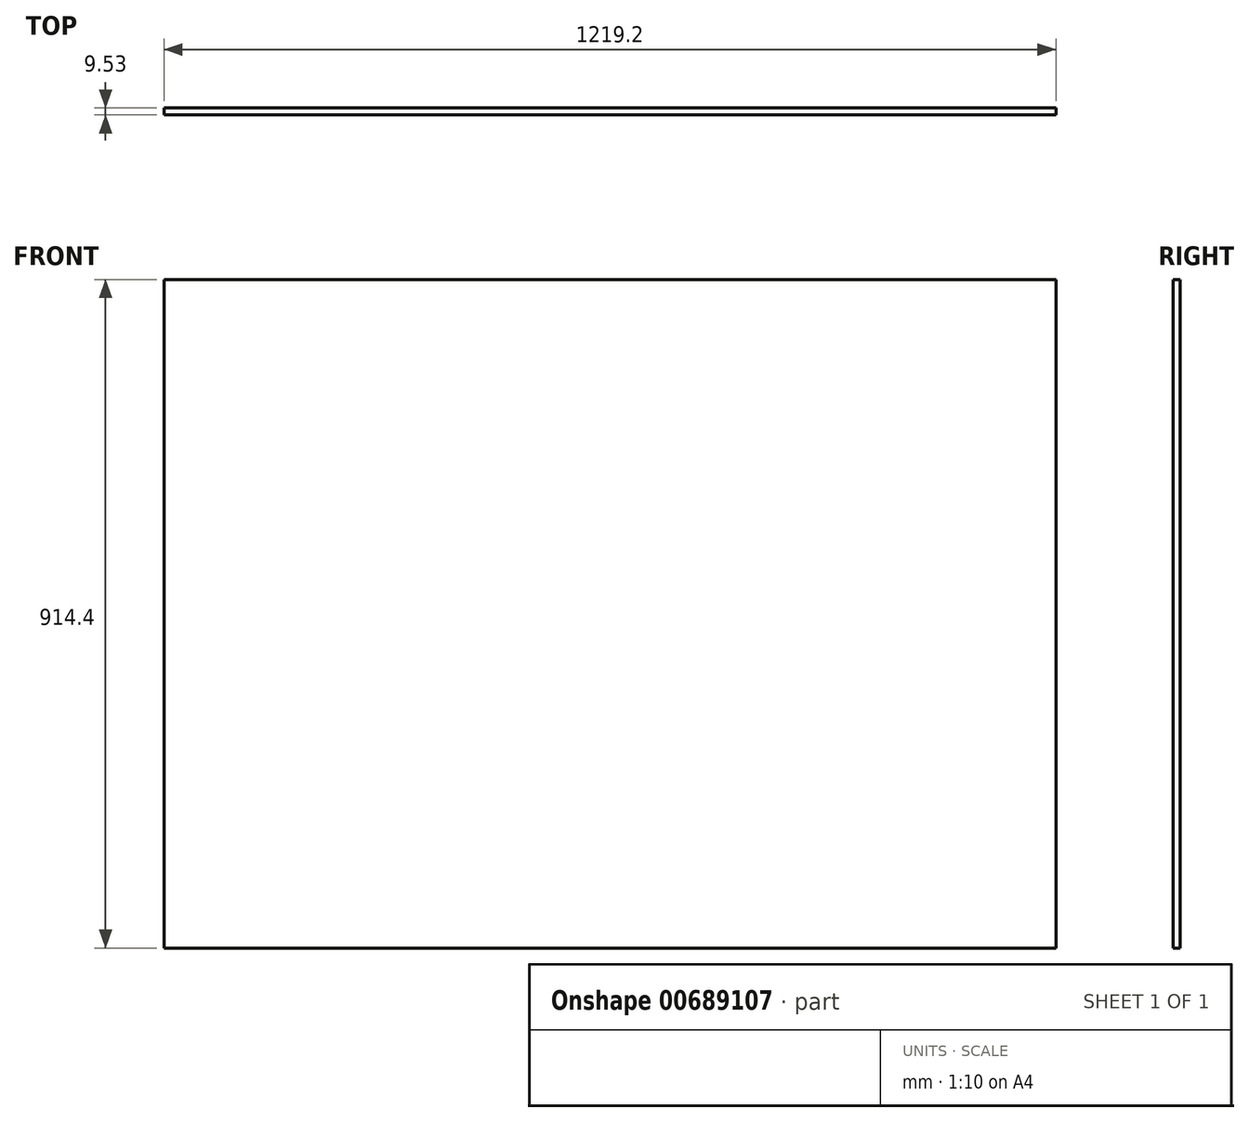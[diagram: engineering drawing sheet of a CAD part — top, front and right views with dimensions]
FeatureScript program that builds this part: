
annotation { "Feature Type Name" : "Feature", "Feature Type Description" : "" }
export const myFeature = defineFeature(function(context is Context, id is Id, definition is map)
    precondition{}
    {
        {
            var Q0;
            Q0=qCreatedBy(makeId("Front.planeOp"),FACE);
            var sketch = newSketch(context, id + "F0", { "sketchPlane" : qUnion([Q0])});
            skLineSegment(sketch, "E0.bottom", {"start": v(-609.6, 457.2) * mm, "end": v(609.6, 457.2) * mm});
            skLineSegment(sketch, "E0.top", {"start": v(-609.6, -457.2) * mm, "end": v(609.6, -457.2) * mm});
            skLineSegment(sketch, "E0.left", {"start": v(-609.6, 457.2) * mm, "end": v(-609.6, -457.2) * mm});
            skLineSegment(sketch, "E0.right", {"start": v(609.6, 457.2) * mm, "end": v(609.6, -457.2) * mm});
            skSolve(sketch);
        }
        {
            var Q0;
            Q0=makeQuery(id+"F0.imprint","IMPRINT",FACE,{"disambiguationData":[TD([[makeQuery(id+"F0.imprint","IMPRINT",EDGE,{"derivedFrom":sQuery(id+"F0.wireOp",EDGE,"E0.bottom")}),-1.0]])]});
            extrude(context, id + "F1", {"entities" : qUnion([Q0]), "depth" : 9.52 * mm, "offsetDistance" : 25.4 * mm});
        }
    });
